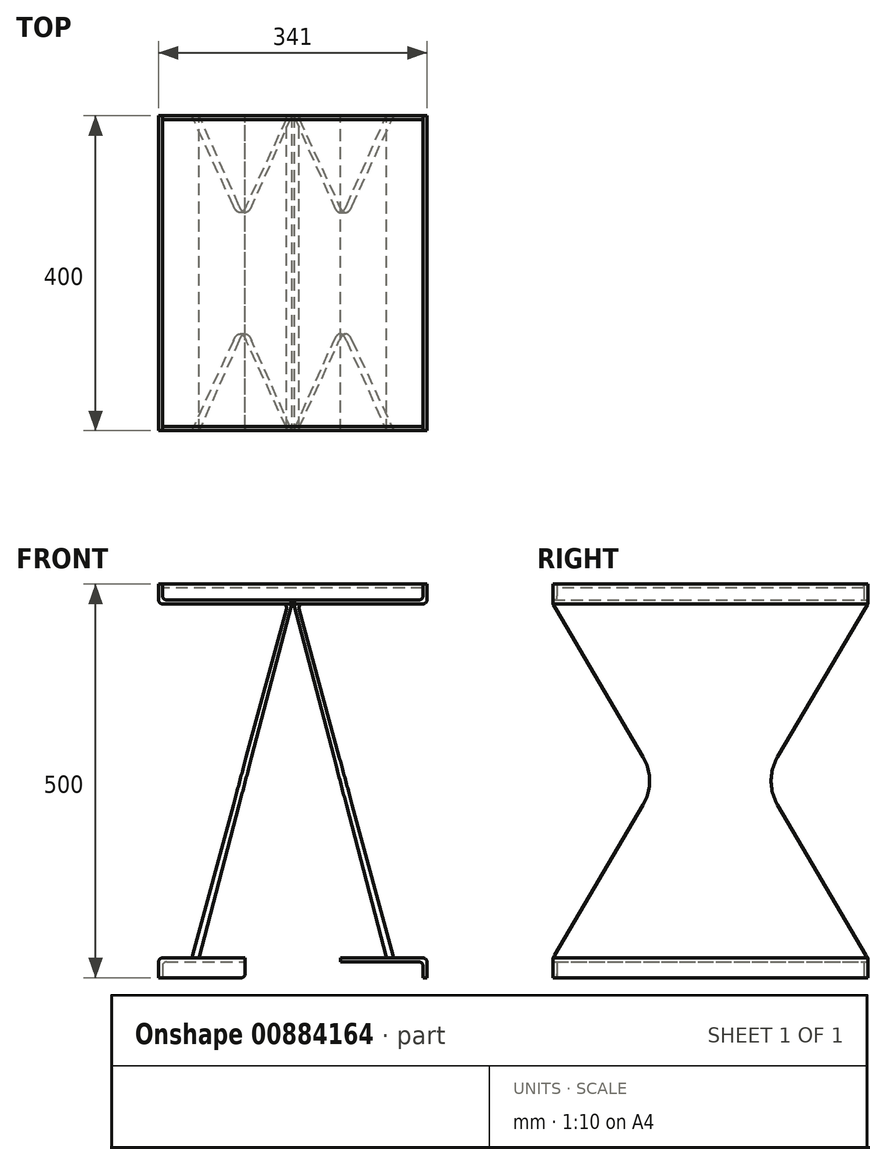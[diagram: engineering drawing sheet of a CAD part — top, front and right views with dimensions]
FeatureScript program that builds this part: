
annotation { "Feature Type Name" : "Feature", "Feature Type Description" : "" }
export const myFeature = defineFeature(function(context is Context, id is Id, definition is map)
    precondition{}
    {
        {
            var Q0;
            Q0=qCreatedBy(makeId("Front.planeOp"),FACE);
            var sketch = newSketch(context, id + "F0", { "sketchPlane" : qUnion([Q0])});
            skLineSegment(sketch, "E0", {"start": v(0, 0) * mm, "end": v(-170.5, 0) * mm, "construction": true});
            skLineSegment(sketch, "E1", {"start": v(-170.5, 0) * mm, "end": v(-170.5, -500) * mm, "construction": true});
            skLineSegment(sketch, "E2", {"start": v(-170.5, -500) * mm, "end": v(0, -500) * mm, "construction": true});
            skLineSegment(sketch, "E3", {"start": v(0, -500) * mm, "end": v(0, 0) * mm, "construction": true});
            skLineSegment(sketch, "E4.MirrorCS", {"start": v(0, 0) * mm, "end": v(170.5, 0) * mm, "construction": true});
            skLineSegment(sketch, "E5.MirrorCS", {"start": v(170.5, 0) * mm, "end": v(170.5, -500) * mm, "construction": true});
            skLineSegment(sketch, "E6.MirrorCS", {"start": v(170.5, -500) * mm, "end": v(0, -500) * mm, "construction": true});
            skLineSegment(sketch, "E7", {"start": v(170.5, -500) * mm, "end": v(0, 0) * mm});
            skLineSegment(sketch, "E8.0", {"start": v(165.77, -501.61) * mm, "end": v(0, -15.5) * mm});
            skLineSegment(sketch, "E9.0", {"start": v(0, -20) * mm, "end": v(-170.5, -20) * mm, "construction": true});
            skLineSegment(sketch, "E10.0", {"start": v(-165.5, 0) * mm, "end": v(-165.5, -500) * mm, "construction": true});
            skLineSegment(sketch, "E11.0", {"start": v(0, -25) * mm, "end": v(-170.5, -25) * mm, "construction": true});
            skLineSegment(sketch, "E12.0", {"start": v(-125.5, 0) * mm, "end": v(-125.5, -500) * mm, "construction": true});
            skLineSegment(sketch, "E13", {"start": v(0, -20) * mm, "end": v(-125.5, -500) * mm, "construction": true});
            skSolve(sketch);
        }
        {
            var Q0;
            Q0=qCreatedBy(makeId("Front.planeOp"),FACE);
            var sketch = newSketch(context, id + "F1", { "sketchPlane" : qUnion([Q0])});
            skLineSegment(sketch, "E14.2", {"start": v(0, -20) * mm, "end": v(-165.5, -20) * mm});
            skLineSegment(sketch, "E14.4", {"start": v(-165.5, 0) * mm, "end": v(-165.5, -20) * mm});
            skLineSegment(sketch, "E14.5", {"start": v(-170.5, 0) * mm, "end": v(-170.5, -25) * mm});
            skPoint(sketch, "E15.orphan", {"position": v(0, -20) * mm});
            skPoint(sketch, "E16.orphan", {"position": v(0, -25) * mm});
            skPoint(sketch, "E17.orphan", {"position": v(-170.5, -20) * mm});
            skLineSegment(sketch, "E18", {"start": v(-170.5, 0) * mm, "end": v(-165.5, 0) * mm});
            skPoint(sketch, "E19.orphan", {"position": v(-170.5, -500) * mm});
            skLineSegment(sketch, "E20.0", {"start": v(0, -20) * mm, "end": v(-118.96, -475) * mm});
            skLineSegment(sketch, "E21.0", {"start": v(-165.5, -480) * mm, "end": v(-60.5, -480) * mm});
            skLineSegment(sketch, "E22.0", {"start": v(-170.5, -500) * mm, "end": v(-165.5, -500) * mm});
            skLineSegment(sketch, "E23.trimOffspring", {"start": v(-6.46, -25) * mm, "end": v(-170.5, -25) * mm});
            skLineSegment(sketch, "E24.trimOffspring", {"start": v(-6.46, -25) * mm, "end": v(-128.05, -475) * mm});
            skLineSegment(sketch, "E25", {"start": v(-170.5, -500) * mm, "end": v(-170.5, -475) * mm});
            skPoint(sketch, "E26.orphan", {"position": v(-165.5, -500) * mm});
            skLineSegment(sketch, "E27.0", {"start": v(-170.5, -475) * mm, "end": v(-128.05, -475) * mm});
            skPoint(sketch, "E28.orphan", {"position": v(0, -500) * mm});
            skLineSegment(sketch, "E29.trimOffspring", {"start": v(-165.5, -480) * mm, "end": v(-165.5, -500) * mm});
            skPoint(sketch, "E30.orphan", {"position": v(-125.5, -500) * mm});
            skLineSegment(sketch, "E31.0", {"start": v(-170.5, -500) * mm, "end": v(-165.5, -500) * mm, "construction": true});
            skLineSegment(sketch, "E32.1", {"start": v(-60.5, -475) * mm, "end": v(-60.5, -480) * mm});
            skLineSegment(sketch, "E33.trimOffspring", {"start": v(-118.96, -475) * mm, "end": v(-60.5, -475) * mm});
            skLineSegment(sketch, "E34", {"start": v(0, -20) * mm, "end": v(0, -35.48) * mm, "construction": true});
            skLineSegment(sketch, "E35", {"start": v(-170.5, -25) * mm, "end": v(-170.5, -475) * mm, "construction": true});
            skSolve(sketch);
        }
        {
            var Q0;
            Q0=qSketchRegion(id+"F1",true);
            extrude(context, id + "F2", {"entities" : qUnion([Q0]), "depth" : 400 * mm, "offsetDistance" : 25 * mm});
        }
        {
            var Q0;
            Q0=qCreatedBy(makeId("Right.planeOp"),FACE);
            var sketch = newSketch(context, id + "F3", { "sketchPlane" : qUnion([Q0])});
            skLineSegment(sketch, "E36.0", {"start": v(-400, -25) * mm, "end": v(0, -25) * mm, "construction": true});
            skLineSegment(sketch, "E36.1", {"start": v(-400, -475) * mm, "end": v(0, -475) * mm, "construction": true});
            skLineSegment(sketch, "E37", {"start": v(-200, -25) * mm, "end": v(-200, -475) * mm, "construction": true});
            skLineSegment(sketch, "E38", {"start": v(-200, -250) * mm, "end": v(135.97, -250) * mm, "construction": true});
            skLineSegment(sketch, "E39", {"start": v(0, -25) * mm, "end": v(-132.5, -250) * mm});
            skLineSegment(sketch, "E40", {"start": v(-132.5, -250) * mm, "end": v(0, -475) * mm});
            skLineSegment(sketch, "E41.MirrorCS", {"start": v(-400, -25) * mm, "end": v(-267.5, -250) * mm});
            skLineSegment(sketch, "E42.MirrorCS", {"start": v(-267.5, -250) * mm, "end": v(-400, -475) * mm});
            skLineSegment(sketch, "E43", {"start": v(0, -25) * mm, "end": v(162.07, -25) * mm});
            skLineSegment(sketch, "E44", {"start": v(162.07, -25) * mm, "end": v(162.07, -475) * mm});
            skLineSegment(sketch, "E45", {"start": v(162.07, -475) * mm, "end": v(0, -475) * mm});
            skLineSegment(sketch, "E46.MirrorCS", {"start": v(-400, -25) * mm, "end": v(-562.07, -25) * mm});
            skLineSegment(sketch, "E47.MirrorCS", {"start": v(-562.07, -475) * mm, "end": v(-400, -475) * mm});
            skLineSegment(sketch, "E48.MirrorCS", {"start": v(-562.07, -25) * mm, "end": v(-562.07, -475) * mm});
            skSolve(sketch);
        }
        {
            var Q0;
            Q0=qSketchRegion(id+"F3",true);
            extrude(context, id + "F4", {"entities" : qUnion([Q0]), "operationType" : NewBodyOperationType.REMOVE, "oppositeDirection" : true, "depth" : 784 * mm, "offsetDistance" : 25 * mm});
        }
        {
            var Q0;
            Q0=makeQuery(id+"F2.opExtrude","SWEPT_EDGE",EDGE,{"disambiguationData":[OSD([sQuery(id+"F1.wireOp",EDGE,"E23.trimOffspring"),sQuery(id+"F1.wireOp",EDGE,"E24.trimOffspring")])]});
            var Q1;
            Q1=makeQuery(id+"F2.opExtrude","SWEPT_EDGE",EDGE,{"disambiguationData":[OSD([sQuery(id+"F1.wireOp",EDGE,"E14.2"),sQuery(id+"F1.wireOp",EDGE,"E20.0")])]});
            var Q2;
            Q2=makeQuery(id+"F2.opExtrude","SWEPT_EDGE",EDGE,{"disambiguationData":[OSD([sQuery(id+"F1.wireOp",EDGE,"E14.5"),sQuery(id+"F1.wireOp",EDGE,"E23.trimOffspring")])]});
            var Q3;
            Q3=makeQuery(id+"F2.opExtrude","SWEPT_EDGE",EDGE,{"disambiguationData":[OSD([sQuery(id+"F1.wireOp",EDGE,"E14.2"),sQuery(id+"F1.wireOp",EDGE,"E14.4")])]});
            var Q4;
            Q4=makeQuery(id+"F2.opExtrude","SWEPT_EDGE",EDGE,{"disambiguationData":[OSD([sQuery(id+"F1.wireOp",EDGE,"E24.trimOffspring"),sQuery(id+"F1.wireOp",EDGE,"E27.0")])]});
            var Q5;
            Q5=makeQuery(id+"F2.opExtrude","SWEPT_EDGE",EDGE,{"disambiguationData":[OSD([sQuery(id+"F1.wireOp",EDGE,"E25"),sQuery(id+"F1.wireOp",EDGE,"E27.0")])]});
            var Q6;
            Q6=makeQuery(id+"F2.opExtrude","SWEPT_EDGE",EDGE,{"disambiguationData":[OSD([sQuery(id+"F1.wireOp",EDGE,"E21.0"),sQuery(id+"F1.wireOp",EDGE,"E29.trimOffspring")])]});
            fillet(context, id + "F5", {"entities" : qUnion([Q0, Q1, Q2, Q3, Q4, Q5, Q6]), "radius" : 5 * mm, "tangentPropagation" : true, "allowEdgeOverflow" : false});
        }
        {
            var Q0;
            Q0=makeQuery(id+"F4.boolean.opBoolean","COPY",EDGE,{"derivedFrom":makeQuery(id+"F4.opExtrude","SWEPT_EDGE",EDGE,{"disambiguationData":[OSD([sQuery(id+"F3.wireOp",EDGE,"E39"),sQuery(id+"F3.wireOp",EDGE,"E40")])]})});
            var Q1;
            Q1=makeQuery(id+"F4.boolean.opBoolean","COPY",EDGE,{"derivedFrom":makeQuery(id+"F4.opExtrude","SWEPT_EDGE",EDGE,{"disambiguationData":[OSD([sQuery(id+"F3.wireOp",EDGE,"E41.MirrorCS"),sQuery(id+"F3.wireOp",EDGE,"E42.MirrorCS")])]})});
            fillet(context, id + "F6", {"entities" : qUnion([Q0, Q1]), "radius" : 60 * mm, "tangentPropagation" : true, "allowEdgeOverflow" : false});
        }
        {
            var Q0;
            Q0=makeQuery(id+"F2.opExtrude","SWEPT_BODY",BODY,{"disambiguationData":[OSD([sQuery(id+"F1.wireOp",EDGE,"E14.2"),sQuery(id+"F1.wireOp",EDGE,"E14.5"),sQuery(id+"F1.wireOp",EDGE,"E18"),sQuery(id+"F1.wireOp",EDGE,"E20.0"),sQuery(id+"F1.wireOp",EDGE,"E21.0"),sQuery(id+"F1.wireOp",EDGE,"E23.trimOffspring"),sQuery(id+"F1.wireOp",EDGE,"E24.trimOffspring"),sQuery(id+"F1.wireOp",EDGE,"E25"),sQuery(id+"F1.wireOp",EDGE,"E27.0"),sQuery(id+"F1.wireOp",EDGE,"E14.4"),sQuery(id+"F1.wireOp",EDGE,"E29.trimOffspring"),sQuery(id+"F1.wireOp",EDGE,"E22.0"),sQuery(id+"F1.wireOp",EDGE,"E32.1"),sQuery(id+"F1.wireOp",EDGE,"E33.trimOffspring")])]});
            var Q1;
            Q1=qCreatedBy(makeId("Right.planeOp"),FACE);
            mirror(context, id + "F7", {"entities" : qUnion([Q0]), "mirrorPlane" : qUnion([Q1])});
        }
        {
            var Q0;
            Q0=qCreatedBy(makeId("Front.planeOp"),FACE);
            var sketch = newSketch(context, id + "F8", { "sketchPlane" : qUnion([Q0])});
            skLineSegment(sketch, "E49.0", {"start": v(-165.5, 0) * mm, "end": v(-165.5, -15) * mm});
            skArc(sketch, "E49.1", {"start": v(-160.5, -20) * mm, "mid": v(-164.04, -18.54) * mm, "end": v(-165.5, -15) * mm});
            skLineSegment(sketch, "E49.2", {"start": v(-6.48, -20) * mm, "end": v(-160.5, -20) * mm});
            skLineSegment(sketch, "E49.3", {"start": v(-6.48, -20) * mm, "end": v(160.5, -20) * mm});
            skArc(sketch, "E49.4", {"start": v(160.5, -20) * mm, "mid": v(164.04, -18.54) * mm, "end": v(165.5, -15) * mm});
            skLineSegment(sketch, "E49.5", {"start": v(165.5, 0) * mm, "end": v(165.5, -15) * mm});
            skPoint(sketch, "E50.orphan", {"position": v(6.48, -20) * mm});
            skLineSegment(sketch, "E51", {"start": v(165.5, 0) * mm, "end": v(-165.5, 0) * mm});
            skSolve(sketch);
        }
        {
            var Q0;
            Q0 = qSketchRegion(id + "F8", true);
            extrude(context, id + "F9", {"entities" : qUnion([Q0]), "depth" : 5 * mm, "offsetDistance" : 25 * mm});
        }
        {
            var Q0;
            {var subQ0=sQuery(id+"F1.wireOp",EDGE,"E18");var subQ1=sQuery(id+"F1.wireOp",EDGE,"E14.5");var subQ2=sQuery(id+"F1.wireOp",EDGE,"E20.0");var subQ3=sQuery(id+"F1.wireOp",EDGE,"E14.2");var subQ4=sQuery(id+"F1.wireOp",EDGE,"E14.4");var subQ5=sQuery(id+"F1.wireOp",EDGE,"E23.trimOffspring");var subQ6=sQuery(id+"F1.wireOp",EDGE,"E24.trimOffspring");Q0=makeQuery(id+"F4.boolean.opBoolean","SPLIT",FACE,{"disambiguationData":[TD([makeQuery(id+"F2.opExtrude","SWEPT_FACE",FACE,{"disambiguationData":[OSD([subQ3])]})])],"derivedFrom":makeQuery(id+"F2.opExtrude","CAP_FACE",FACE,{"disambiguationData":[OSD([subQ3,subQ1,subQ0,subQ2,sQuery(id+"F1.wireOp",EDGE,"E21.0"),subQ5,subQ6,sQuery(id+"F1.wireOp",EDGE,"E25"),sQuery(id+"F1.wireOp",EDGE,"E27.0"),subQ4,sQuery(id+"F1.wireOp",EDGE,"E29.trimOffspring"),sQuery(id+"F1.wireOp",EDGE,"E22.0"),sQuery(id+"F1.wireOp",EDGE,"E32.1"),sQuery(id+"F1.wireOp",EDGE,"E33.trimOffspring")])],"isStart":false})});}
            var sketch = newSketch(context, id + "F10", { "sketchPlane" : qUnion([Q0])});
            skLineSegment(sketch, "E52.0", {"start": v(-165.5, 0) * mm, "end": v(-165.5, -15) * mm});
            skArc(sketch, "E52.1", {"start": v(-160.5, -20) * mm, "mid": v(-164.04, -18.54) * mm, "end": v(-165.5, -15) * mm});
            skLineSegment(sketch, "E52.2", {"start": v(-6.48, -20) * mm, "end": v(-160.5, -20) * mm});
            skLineSegment(sketch, "E52.3", {"start": v(-6.48, -20) * mm, "end": v(160.5, -20) * mm});
            skArc(sketch, "E52.4", {"start": v(160.5, -20) * mm, "mid": v(164.04, -18.54) * mm, "end": v(165.5, -15) * mm});
            skLineSegment(sketch, "E52.5", {"start": v(165.5, 0) * mm, "end": v(165.5, -15) * mm});
            skPoint(sketch, "E53.orphan", {"position": v(6.48, -20) * mm});
            skLineSegment(sketch, "E54", {"start": v(-165.5, 0) * mm, "end": v(165.5, 0) * mm});
            skSolve(sketch);
        }
        {
            var Q0;
            Q0 = qSketchRegion(id + "F10", true);
            extrude(context, id + "F11", {"entities" : qUnion([Q0]), "oppositeDirection" : true, "depth" : 5 * mm, "offsetDistance" : 25 * mm});
        }
        {
            var Q0;
            Q0=makeQuery(id+"F11.opExtrude","CAP_FACE",FACE,{"disambiguationData":[OSD([sQuery(id+"F10.wireOp",EDGE,"E52.0"),sQuery(id+"F10.wireOp",EDGE,"E52.1"),sQuery(id+"F10.wireOp",EDGE,"E52.2"),sQuery(id+"F10.wireOp",EDGE,"E52.3"),sQuery(id+"F10.wireOp",EDGE,"E52.4"),sQuery(id+"F10.wireOp",EDGE,"E52.5"),sQuery(id+"F10.wireOp",EDGE,"E54")])],"isStart":false});
            var sketch = newSketch(context, id + "F12", { "sketchPlane" : qUnion([Q0])});
            skSolve(sketch);
        }
        {
            var Q0;
            Q0=makeQuery(id+"F12.imprint","IMPRINT",FACE,{"disambiguationData":[TD([[makeQuery(id+"F12.imprint","IMPRINT",EDGE,{"derivedFrom":makeQuery(id+"F11.opExtrude","CAP_EDGE",EDGE,{"disambiguationData":[OSD([sQuery(id+"F10.wireOp",EDGE,"E52.0")])],"isStart":false})}),-1.0]])]});
            var sketch = newSketch(context, id + "F13", { "sketchPlane" : qUnion([Q0])});
            skLineSegment(sketch, "E55.0", {"start": v(165.5, 0) * mm, "end": v(-165.5, 0) * mm});
            skLineSegment(sketch, "E56.0", {"start": v(165.5, -5) * mm, "end": v(-165.5, -5) * mm});
            skLineSegment(sketch, "E57.0", {"start": v(165.5, 0) * mm, "end": v(165.5, -5) * mm});
            skLineSegment(sketch, "E57.1", {"start": v(-165.5, 0) * mm, "end": v(-165.5, -5) * mm});
            skPoint(sketch, "E58.orphan", {"position": v(-165.5, -15) * mm});
            skPoint(sketch, "E59.orphan", {"position": v(165.5, -15) * mm});
            skSolve(sketch);
        }
        {
            var Q0;
            Q0 = qSketchRegion(id + "F13", true);
            var Q1;
            Q1=makeQuery(id+"F9.opExtrude","CAP_FACE",FACE,{"disambiguationData":[OSD([sQuery(id+"F8.wireOp",EDGE,"E49.0"),sQuery(id+"F8.wireOp",EDGE,"E49.1"),sQuery(id+"F8.wireOp",EDGE,"E49.2"),sQuery(id+"F8.wireOp",EDGE,"E49.3"),sQuery(id+"F8.wireOp",EDGE,"E49.4"),sQuery(id+"F8.wireOp",EDGE,"E49.5"),sQuery(id+"F8.wireOp",EDGE,"E51")])],"isStart":false});
            extrude(context, id + "F14", {"entities" : qUnion([Q0]), "endBound" : BoundingType.UP_TO_SURFACE, "depth" : 25 * mm, "endBoundEntityFace" : qUnion([Q1]), "offsetDistance" : 25 * mm});
        }
        {
            var Q0;
            {var subQ0=sQuery(id+"F1.wireOp",EDGE,"E25");var subQ1=sQuery(id+"F1.wireOp",EDGE,"E24.trimOffspring");var subQ2=sQuery(id+"F1.wireOp",EDGE,"E21.0");var subQ3=sQuery(id+"F1.wireOp",EDGE,"E20.0");var subQ4=sQuery(id+"F1.wireOp",EDGE,"E27.0");var subQ5=sQuery(id+"F1.wireOp",EDGE,"E29.trimOffspring");var subQ6=sQuery(id+"F1.wireOp",EDGE,"E22.0");var subQ7=sQuery(id+"F1.wireOp",EDGE,"E32.1");var subQ8=sQuery(id+"F1.wireOp",EDGE,"E33.trimOffspring");Q0=makeQuery(id+"F4.boolean.opBoolean","SPLIT",FACE,{"disambiguationData":[TD([makeQuery(id+"F2.opExtrude","SWEPT_FACE",FACE,{"disambiguationData":[OSD([subQ2])]})])],"derivedFrom":makeQuery(id+"F2.opExtrude","CAP_FACE",FACE,{"disambiguationData":[OSD([sQuery(id+"F1.wireOp",EDGE,"E14.2"),sQuery(id+"F1.wireOp",EDGE,"E14.5"),sQuery(id+"F1.wireOp",EDGE,"E18"),subQ3,subQ2,sQuery(id+"F1.wireOp",EDGE,"E23.trimOffspring"),subQ1,subQ0,subQ4,sQuery(id+"F1.wireOp",EDGE,"E14.4"),subQ5,subQ6,subQ7,subQ8])],"isStart":true})});}
            var sketch = newSketch(context, id + "F15", { "sketchPlane" : qUnion([Q0])});
            skArc(sketch, "E60.0", {"start": v(160.5, -480) * mm, "mid": v(164.04, -481.46) * mm, "end": v(165.5, -485) * mm});
            skLineSegment(sketch, "E60.1", {"start": v(160.5, -480) * mm, "end": v(60.5, -480) * mm});
            skLineSegment(sketch, "E60.2", {"start": v(60.5, -480) * mm, "end": v(60.5, -495) * mm});
            skLineSegment(sketch, "E60.3", {"start": v(165.5, -485) * mm, "end": v(165.5, -500) * mm});
            skLineSegment(sketch, "E61", {"start": v(165.5, -500) * mm, "end": v(65.5, -500) * mm});
            skPoint(sketch, "E62.orphan", {"position": v(60.5, -475) * mm});
            skPoint(sketch, "E63.visualSharp", {"position": v(60.5, -500) * mm});
            skArc(sketch, "E63.filletArc", {"start": v(60.5, -495) * mm, "mid": v(61.96, -498.54) * mm, "end": v(65.5, -500) * mm});
            skSolve(sketch);
        }
        {
            var Q0;
            Q0 = qSketchRegion(id + "F15", true);
            extrude(context, id + "F16", {"entities" : qUnion([Q0]), "oppositeDirection" : true, "depth" : 5 * mm, "offsetDistance" : 25 * mm});
        }
        {
            var Q0;
            {var subQ0=sQuery(id+"F1.wireOp",EDGE,"E25");var subQ1=sQuery(id+"F1.wireOp",EDGE,"E24.trimOffspring");var subQ2=sQuery(id+"F1.wireOp",EDGE,"E21.0");var subQ3=sQuery(id+"F1.wireOp",EDGE,"E20.0");var subQ4=sQuery(id+"F1.wireOp",EDGE,"E27.0");var subQ5=sQuery(id+"F1.wireOp",EDGE,"E29.trimOffspring");var subQ6=sQuery(id+"F1.wireOp",EDGE,"E22.0");var subQ7=sQuery(id+"F1.wireOp",EDGE,"E32.1");var subQ8=sQuery(id+"F1.wireOp",EDGE,"E33.trimOffspring");Q0=makeQuery(id+"F4.boolean.opBoolean","SPLIT",FACE,{"disambiguationData":[TD([makeQuery(id+"F2.opExtrude","SWEPT_FACE",FACE,{"disambiguationData":[OSD([subQ2])]})])],"derivedFrom":makeQuery(id+"F2.opExtrude","CAP_FACE",FACE,{"disambiguationData":[OSD([sQuery(id+"F1.wireOp",EDGE,"E14.2"),sQuery(id+"F1.wireOp",EDGE,"E14.5"),sQuery(id+"F1.wireOp",EDGE,"E18"),subQ3,subQ2,sQuery(id+"F1.wireOp",EDGE,"E23.trimOffspring"),subQ1,subQ0,subQ4,sQuery(id+"F1.wireOp",EDGE,"E14.4"),subQ5,subQ6,subQ7,subQ8])],"isStart":false})});}
            var sketch = newSketch(context, id + "F17", { "sketchPlane" : qUnion([Q0])});
            skLineSegment(sketch, "E64.0", {"start": v(-165.5, -485) * mm, "end": v(-165.5, -500) * mm});
            skArc(sketch, "E64.1", {"start": v(-165.5, -485) * mm, "mid": v(-164.04, -481.46) * mm, "end": v(-160.5, -480) * mm});
            skLineSegment(sketch, "E64.2", {"start": v(-160.5, -480) * mm, "end": v(-60.5, -480) * mm});
            skLineSegment(sketch, "E65", {"start": v(-165.5, -500) * mm, "end": v(-65.5, -500) * mm});
            skLineSegment(sketch, "E66", {"start": v(-60.5, -480) * mm, "end": v(-60.5, -495) * mm});
            skArc(sketch, "E67.filletArc", {"start": v(-65.5, -500) * mm, "mid": v(-61.96, -498.54) * mm, "end": v(-60.5, -495) * mm});
            skSolve(sketch);
        }
        {
            var Q0;
            Q0 = qSketchRegion(id + "F17", true);
            extrude(context, id + "F18", {"entities" : qUnion([Q0]), "operationType" : NewBodyOperationType.ADD, "oppositeDirection" : true, "depth" : 5 * mm, "offsetDistance" : 25 * mm});
        }
    });
